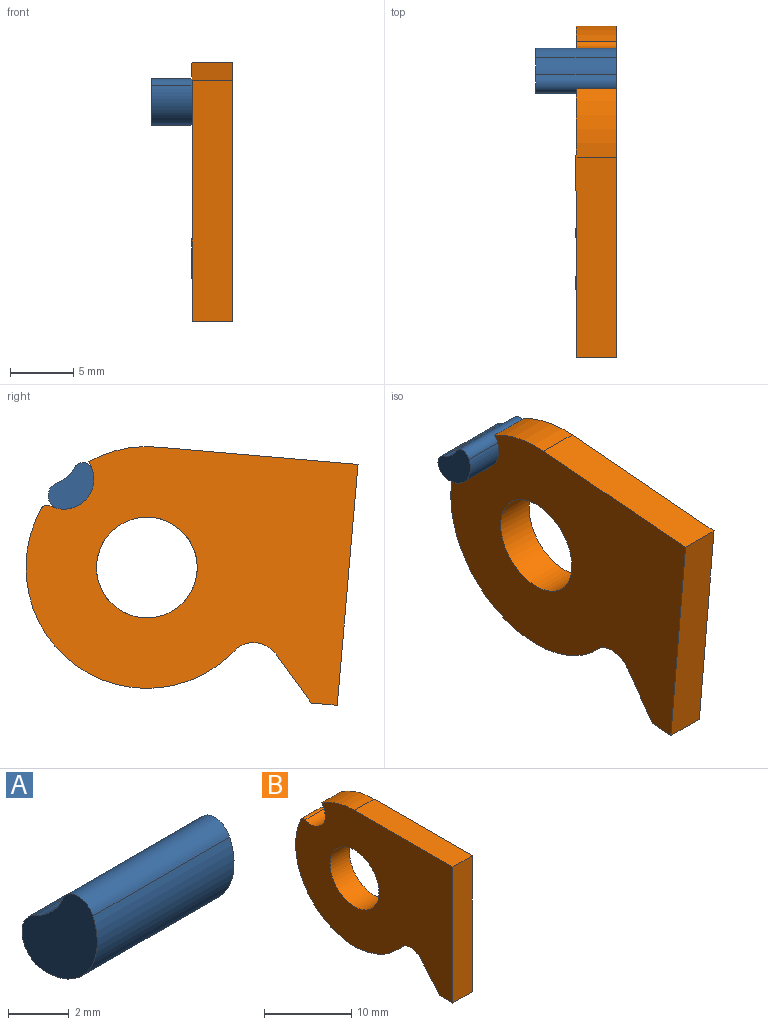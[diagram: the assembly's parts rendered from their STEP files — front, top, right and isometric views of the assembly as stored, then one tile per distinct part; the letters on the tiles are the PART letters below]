
ASSEMBLY  parts=2 mates=1
PART A: 6 faces, bbox 6.4x3.5x3.8 mm
  f0: cylinder r=2.37mm len=6.35mm, axis (-1,0,0), area 30.6mm2, adj f1,f2,f4,f5
  f1: plane 3.79x3.49mm, normal (1,0,0), area 8.6mm2, adj f0,f3,f4,f5
  f2: plane 3.79x3.49mm, normal (-1,0,0), area 8.6mm2, adj f0,f3,f4,f5
  f3: cylinder r=2.41mm len=6.35mm, axis (1,0,0), area 11.6mm2, adj f1,f2,f4,f5
  f4: cylinder r=0.76mm len=6.35mm, axis (-1,0,0), area 11.3mm2, adj f0,f1,f2,f3
  f5: cylinder r=1.07mm len=6.35mm, axis (-1,0,0), area 18.2mm2, adj f0,f1,f2,f3
PART B: 12 faces, bbox 3.2x25.4x19.1 mm
  f0: plane 25.4x19.05mm, normal (1,0,0), area 359.9mm2, adj f2,f3,f4,f5,f6,f7,f8,f9
  f1: plane 25.4x19.05mm, normal (-1,0,0), area 359.9mm2, adj f2,f3,f4,f5,f6,f7,f8,f9
  f2: cylinder r=9.53mm len=5.3mm, axis (1,0,0), area 17.9mm2, adj f0,f1,f3,f8
  f3: plane 15.88x3.18mm, normal (0,0,1), area 50.4mm2, adj f0,f1,f2,f4
  f4: plane 19.05x3.18mm, normal (0,-1,0), area 60.5mm2, adj f0,f1,f3,f5
  f5: plane 3.18x2.05mm, normal (0,0,-1), area 6.5mm2, adj f0,f1,f4,f11
  f6: cylinder r=9.53mm len=17.16mm, axis (1,0,0), area 88.5mm2, adj f0,f1,f9,f10
  f7: cylinder r=3.97mm len=7.94mm, axis (1,0,0), area 79.2mm2, adj f0,f1
  f8: cylinder r=2.37mm len=3.9mm, axis (1,0,0), area 20mm2, adj f0,f1,f2,f9
  f9: cylinder r=0.51mm len=3.18mm, axis (1,0,0), area 2.5mm2, adj f0,f1,f6,f8
  f10: cylinder r=2.18mm len=3.18mm, axis (1,0,0), area 10.9mm2, adj f0,f1,f6,f11
  f11: plane 3.61x3.18mm, normal (0,0.76,-0.65), area 15.1mm2, adj f0,f1,f5,f10
PLACE A rot(axis=(1,0,0),4.9deg) t=(-8.64,-10.05,16.79)mm
PLACE B rot(axis=(1,0,0),4.9deg) t=(-5.47,12.59,-15.68)mm
MATE revolute B.f8 <-> A.f0  axis (1,0,0) through (-2.29,-10.05,16.79)mm
